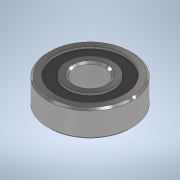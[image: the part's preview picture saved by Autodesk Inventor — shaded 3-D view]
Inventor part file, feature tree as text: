
AUTODESK INVENTOR PART (.ipt)
format: ipt  version: 2021 (Build 250183000, 183)  size: 148,480 bytes
history: native  units: mm
features: extrude x2, sketch x2, plane x1, chamfer x1
ambient origin geometry x8: Origin, YZ Plane, XZ Plane, XY Plane, X Axis, Y Axis, Z Axis, Center Point
bodies: Solid1 (feature_tree)
feature tree (6):
  extrude  "Extrusion1"  Depth=8.0mm
  plane  "Work Plane1"
  extrude  "Extrusion2"  Depth=0.5mm
  chamfer  "Chamfer1"  Distance=7.0mm
  sketch  "Sketch1"  dims[d0=22.0mm d1=8.0mm]
  sketch  "Sketch2"  dims[d2=2.0mm d3=2.0mm d4=7.0mm d5=0.0mm d6=-0.5mm d7=6.0mm d8=0.0mm d9=0.5mm d10=2.0mm d11=45.0deg]
